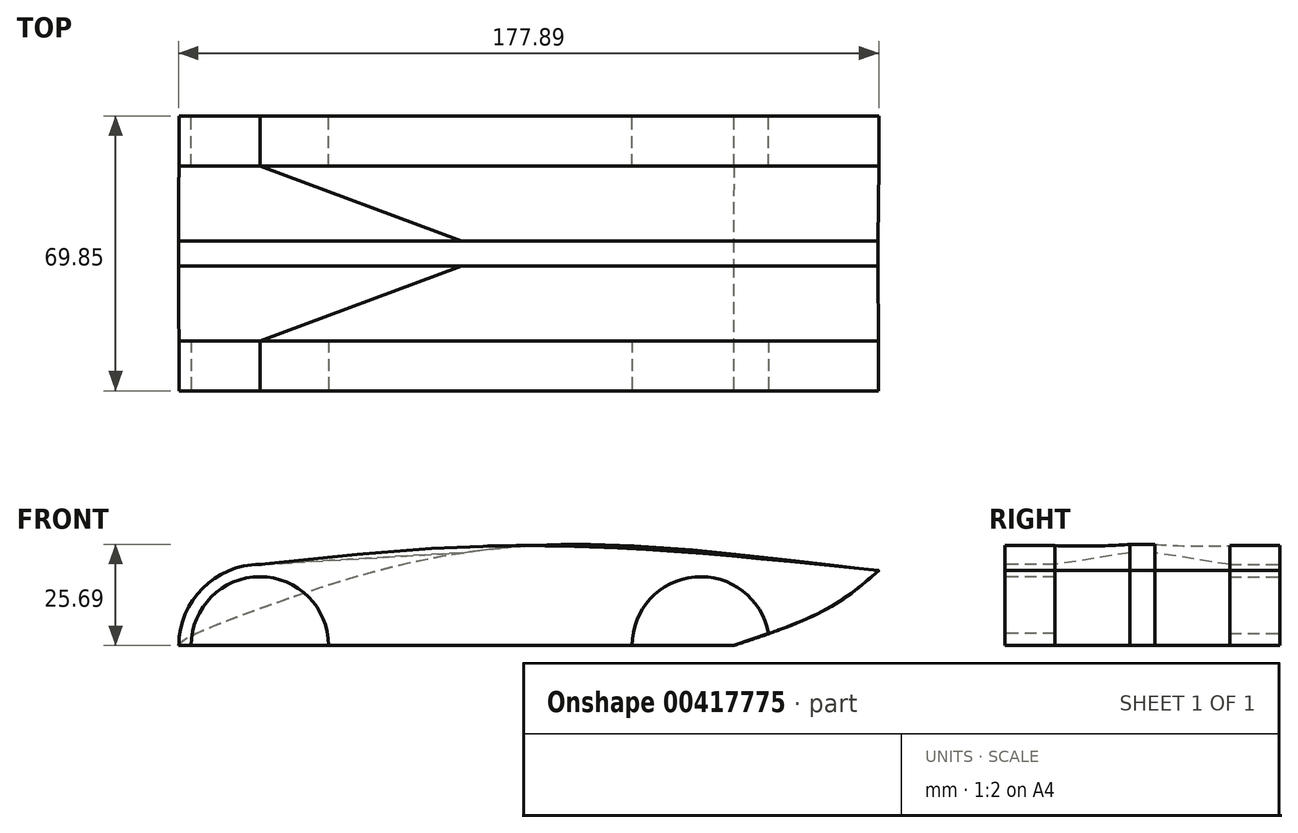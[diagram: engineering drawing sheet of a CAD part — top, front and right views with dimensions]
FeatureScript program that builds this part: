
annotation { "Feature Type Name" : "Feature", "Feature Type Description" : "" }
export const myFeature = defineFeature(function(context is Context, id is Id, definition is map)
    precondition{}
    {
        {
            var Q0;
            Q0=qCreatedBy(makeId("Front.planeOp"),FACE);
            var sketch = newSketch(context, id + "F0", { "sketchPlane" : qUnion([Q0])});
            skPoint(sketch, "E0.middle", {"position": v(0, 0) * mm});
            skArc(sketch, "E1", {"start": v(-50.86, -9.53) * mm, "mid": v(-68.33, 7.94) * mm, "end": v(-85.79, -9.53) * mm});
            skArc(sketch, "E2", {"start": v(60.88, -6.49) * mm, "mid": v(42.16, 7.87) * mm, "end": v(26.23, -9.52) * mm});
            skArc(sketch, "E3", {"start": v(-68.33, 11.05) * mm, "mid": v(-82.87, 5.02) * mm, "end": v(-88.9, -9.53) * mm});
            skFitSpline(sketch, "E4", {"points": [v(-68.33, 11.05) * mm, v(0, 15.84) * mm, v(88.9, 9.53) * mm], "startDerivative": vector(141.46, 15.42) * mm, "endDerivative": vector(172.31, -17.74) * mm});
            skFitSpline(sketch, "E5", {"points": [v(52.1, -9.53) * mm, v(76.2, 0) * mm, v(88.9, 9.53) * mm], "startDerivative": vector(46.9, 15.66) * mm, "endDerivative": vector(25.85, 22.73) * mm});
            skPoint(sketch, "E6.orphan", {"position": v(-88.9, 9.52) * mm});
            skPoint(sketch, "E7.trimOffspring.end.orphan", {"position": v(-88.9, -9.53) * mm});
            skLineSegment(sketch, "E8.trimOffspring", {"start": v(23.11, -9.52) * mm, "end": v(-47.75, -9.53) * mm});
            skPoint(sketch, "E0.bottom.start.orphan", {"position": v(88.9, -9.52) * mm});
            skPoint(sketch, "E9.orphan", {"position": v(88.9, 11.05) * mm});
            skLineSegment(sketch, "E10", {"start": v(-47.75, -9.53) * mm, "end": v(-88.9, -9.53) * mm});
            skLineSegment(sketch, "E11", {"start": v(23.11, -9.52) * mm, "end": v(52.1, -9.52) * mm});
            skLineSegment(sketch, "E12", {"start": v(63.86, -5.46) * mm, "end": v(52.1, -9.52) * mm});
            skSolve(sketch);
        }
        {
            var Q0;
            Q0=qCreatedBy(makeId("Front.planeOp"),FACE);
            cPlane(context, id + "F1", {"entities" : qUnion([Q0]), "cplaneType" : CPlaneType.OFFSET, "offset" : 34.92 * mm, "width" : 152.4 * mm, "height" : 152.4 * mm});
        }
        {
            var Q0;
            Q0=qCreatedBy(id+"F1.planeOp",FACE);
            cPlane(context, id + "F2", {"entities" : qUnion([Q0]), "cplaneType" : CPlaneType.OFFSET, "offset" : 34.92 * mm, "width" : 152.4 * mm, "height" : 152.4 * mm});
        }
        {
            var Q0;
            Q0=qCreatedBy(id+"F2.planeOp",FACE);
            var sketch = newSketch(context, id + "F3", { "sketchPlane" : qUnion([Q0])});
            skArc(sketch, "E13", {"start": v(-68.33, 11.05) * mm, "mid": v(-82.87, 5.03) * mm, "end": v(-88.9, -9.5) * mm});
            skArc(sketch, "E14", {"start": v(-50.86, -9.5) * mm, "mid": v(-68.33, 7.94) * mm, "end": v(-85.79, -9.5) * mm});
            skArc(sketch, "E15", {"start": v(60.88, -6.45) * mm, "mid": v(42.15, 7.87) * mm, "end": v(26.23, -9.5) * mm});
            skFitSpline(sketch, "E16", {"points": [v(-68.33, 11.05) * mm, v(-0.06, 15.86) * mm, v(88.84, 9.54) * mm], "startDerivative": vector(141.46, 15.42) * mm, "endDerivative": vector(172.31, -17.74) * mm});
            skFitSpline(sketch, "E17", {"points": [v(52.03, -9.5) * mm, v(76.13, 0.02) * mm, v(88.84, 9.54) * mm], "startDerivative": vector(46.9, 15.66) * mm, "endDerivative": vector(25.85, 22.73) * mm});
            skLineSegment(sketch, "E18.trimOffspring", {"start": v(23.05, -9.5) * mm, "end": v(-47.82, -9.5) * mm});
            skLineSegment(sketch, "E19", {"start": v(-47.82, -9.5) * mm, "end": v(-88.9, -9.5) * mm});
            skLineSegment(sketch, "E20", {"start": v(23.05, -9.5) * mm, "end": v(52.03, -9.5) * mm});
            skLineSegment(sketch, "E21", {"start": v(52.03, -9.5) * mm, "end": v(63.85, -5.42) * mm});
            skSolve(sketch);
        }
        {
            var Q0;
            Q0=qCreatedBy(id+"F1.planeOp",FACE);
            var sketch = newSketch(context, id + "F4", { "sketchPlane" : qUnion([Q0])});
            skFitSpline(sketch, "E22", {"points": [v(-89, -9.53) * mm, v(-67.74, 0.11) * mm, v(-0.16, 15.83) * mm, v(88.74, 9.52) * mm], "startDerivative": vector(-0.9, 23.46) * mm, "endDerivative": vector(172.31, -17.74) * mm});
            skFitSpline(sketch, "E23", {"points": [v(51.94, -9.53) * mm, v(76.04, 0) * mm, v(88.74, 9.52) * mm], "startDerivative": vector(46.9, 15.66) * mm, "endDerivative": vector(25.85, 22.73) * mm});
            skLineSegment(sketch, "E24.trimOffspring", {"start": v(22.96, -9.53) * mm, "end": v(-47.9, -9.53) * mm});
            skLineSegment(sketch, "E25", {"start": v(-47.9, -9.53) * mm, "end": v(-89, -9.53) * mm});
            skLineSegment(sketch, "E26", {"start": v(22.96, -9.53) * mm, "end": v(51.94, -9.53) * mm});
            skLineSegment(sketch, "E27", {"start": v(51.94, -9.53) * mm, "end": v(63.76, -5.45) * mm});
            skSolve(sketch);
        }
        {
            var Q0;
            Q0=qSketchRegion(id+"F4",true);
            extrude(context, id + "F5", {"entities" : qUnion([Q0]), "endBound" : BoundingType.SYMMETRIC, "oppositeDirection" : true, "depth" : 6.35 * mm});
        }
        {
            var Q0;
            Q0=qSketchRegion(id+"F3",true);
            extrude(context, id + "F6", {"entities" : qUnion([Q0]), "oppositeDirection" : true, "depth" : 12.7 * mm});
        }
        {
            var Q0;
            Q0=qSketchRegion(id+"F0",true);
            extrude(context, id + "F7", {"entities" : qUnion([Q0]), "depth" : 12.7 * mm});
        }
        {
            var Q0;
            Q0=makeQuery(id+"F5.opExtrude","CAP_FACE",FACE,{"disambiguationData":[OSD([sQuery(id+"F4.wireOp",EDGE,"E22"),sQuery(id+"F4.wireOp",EDGE,"E23"),sQuery(id+"F4.wireOp",EDGE,"E24.trimOffspring"),sQuery(id+"F4.wireOp",EDGE,"E25"),sQuery(id+"F4.wireOp",EDGE,"E26"),sQuery(id+"F4.wireOp",EDGE,"E27")])],"isStart":true});
            var Q1;
            Q1=makeQuery(id+"F6.opExtrude","CAP_FACE",FACE,{"disambiguationData":[OSD([sQuery(id+"F3.wireOp",EDGE,"E13"),sQuery(id+"F3.wireOp",EDGE,"E16"),sQuery(id+"F3.wireOp",EDGE,"E17"),sQuery(id+"F3.wireOp",EDGE,"E18.trimOffspring"),sQuery(id+"F3.wireOp",EDGE,"E19"),sQuery(id+"F3.wireOp",EDGE,"E20"),sQuery(id+"F3.wireOp",EDGE,"E21")])],"isStart":false});
            var Q2;
            Q2=makeQuery(id+"F5.opExtrude","CAP_VERTEX",VERTEX,{"disambiguationData":[OSD([sQuery(id+"F4.wireOp",EDGE,"E22"),sQuery(id+"F4.wireOp",EDGE,"E23")])],"isStart":true});
            var Q3;
            Q3=makeQuery(id+"F6.opExtrude","CAP_VERTEX",VERTEX,{"disambiguationData":[OSD([sQuery(id+"F3.wireOp",EDGE,"E16"),sQuery(id+"F3.wireOp",EDGE,"E17")])],"isStart":false});
            loft(context, id + "F8", {"sheetProfilesArray" : [{ "sheetProfileEntities" : qUnion([Q0]) }, { "sheetProfileEntities" : qUnion([Q1]) }], "matchConnections" : true, "connections" : [{ "connectionEntities" : qUnion([Q2, Q3]), "connectionEdgeQueries" : qUnion([]), "connectionEdgeParameters" : [] }]});
        }
        {
            var Q0;
            Q0=makeQuery(id+"F7.opExtrude","CAP_FACE",FACE,{"disambiguationData":[OSD([sQuery(id+"F0.wireOp",EDGE,"E3"),sQuery(id+"F0.wireOp",EDGE,"E4"),sQuery(id+"F0.wireOp",EDGE,"E5"),sQuery(id+"F0.wireOp",EDGE,"E8.trimOffspring"),sQuery(id+"F0.wireOp",EDGE,"E10"),sQuery(id+"F0.wireOp",EDGE,"E11"),sQuery(id+"F0.wireOp",EDGE,"E12")])],"isStart":false});
            var Q1;
            Q1=makeQuery(id+"F5.opExtrude","CAP_FACE",FACE,{"disambiguationData":[OSD([sQuery(id+"F4.wireOp",EDGE,"E22"),sQuery(id+"F4.wireOp",EDGE,"E23"),sQuery(id+"F4.wireOp",EDGE,"E24.trimOffspring"),sQuery(id+"F4.wireOp",EDGE,"E25"),sQuery(id+"F4.wireOp",EDGE,"E26"),sQuery(id+"F4.wireOp",EDGE,"E27")])],"isStart":false});
            var Q2;
            Q2=makeQuery(id+"F7.opExtrude","CAP_VERTEX",VERTEX,{"disambiguationData":[OSD([sQuery(id+"F0.wireOp",EDGE,"E4"),sQuery(id+"F0.wireOp",EDGE,"E5")])],"isStart":false});
            var Q3;
            Q3=makeQuery(id+"F5.opExtrude","CAP_VERTEX",VERTEX,{"disambiguationData":[OSD([sQuery(id+"F4.wireOp",EDGE,"E22"),sQuery(id+"F4.wireOp",EDGE,"E23")])],"isStart":false});
            loft(context, id + "F9", {"sheetProfilesArray" : [{ "sheetProfileEntities" : qUnion([Q0]) }, { "sheetProfileEntities" : qUnion([Q1]) }], "matchConnections" : true, "connections" : [{ "connectionEntities" : qUnion([Q2, Q3]), "connectionEdgeQueries" : qUnion([]), "connectionEdgeParameters" : [] }]});
        }
        {
            var Q0;
            {var subQ0=sQuery(id+"F0.wireOp",EDGE,"E2");Q0=makeQuery(id+"F0.imprint","IMPRINT",FACE,{"disambiguationData":[TD([[makeQuery(id+"F0.imprint","IMPRINT",EDGE,{"derivedFrom":subQ0}),1.0]])]});}
            extrude(context, id + "F10", {"entities" : qUnion([Q0]), "operationType" : NewBodyOperationType.REMOVE, "depth" : 12.7 * mm});
        }
        {
            var Q0;
            {var subQ0=sQuery(id+"F0.wireOp",EDGE,"E1");Q0=makeQuery(id+"F0.imprint","IMPRINT",FACE,{"disambiguationData":[TD([[makeQuery(id+"F0.imprint","IMPRINT",EDGE,{"derivedFrom":subQ0}),1.0]])]});}
            extrude(context, id + "F11", {"entities" : qUnion([Q0]), "operationType" : NewBodyOperationType.REMOVE, "depth" : 12.7 * mm});
        }
        {
            var Q0;
            {var subQ0=sQuery(id+"F3.wireOp",EDGE,"E14");Q0=makeQuery(id+"F3.imprint","IMPRINT",FACE,{"disambiguationData":[TD([[makeQuery(id+"F3.imprint","IMPRINT",EDGE,{"derivedFrom":subQ0}),1.0]])]});}
            extrude(context, id + "F12", {"entities" : qUnion([Q0]), "operationType" : NewBodyOperationType.REMOVE, "oppositeDirection" : true, "depth" : 12.7 * mm});
        }
        {
            var Q0;
            {var subQ0=sQuery(id+"F3.wireOp",EDGE,"E15");Q0=makeQuery(id+"F3.imprint","IMPRINT",FACE,{"disambiguationData":[TD([[makeQuery(id+"F3.imprint","IMPRINT",EDGE,{"derivedFrom":subQ0}),1.0]])]});}
            extrude(context, id + "F13", {"entities" : qUnion([Q0]), "operationType" : NewBodyOperationType.REMOVE, "oppositeDirection" : true, "depth" : 12.7 * mm});
        }
    });
